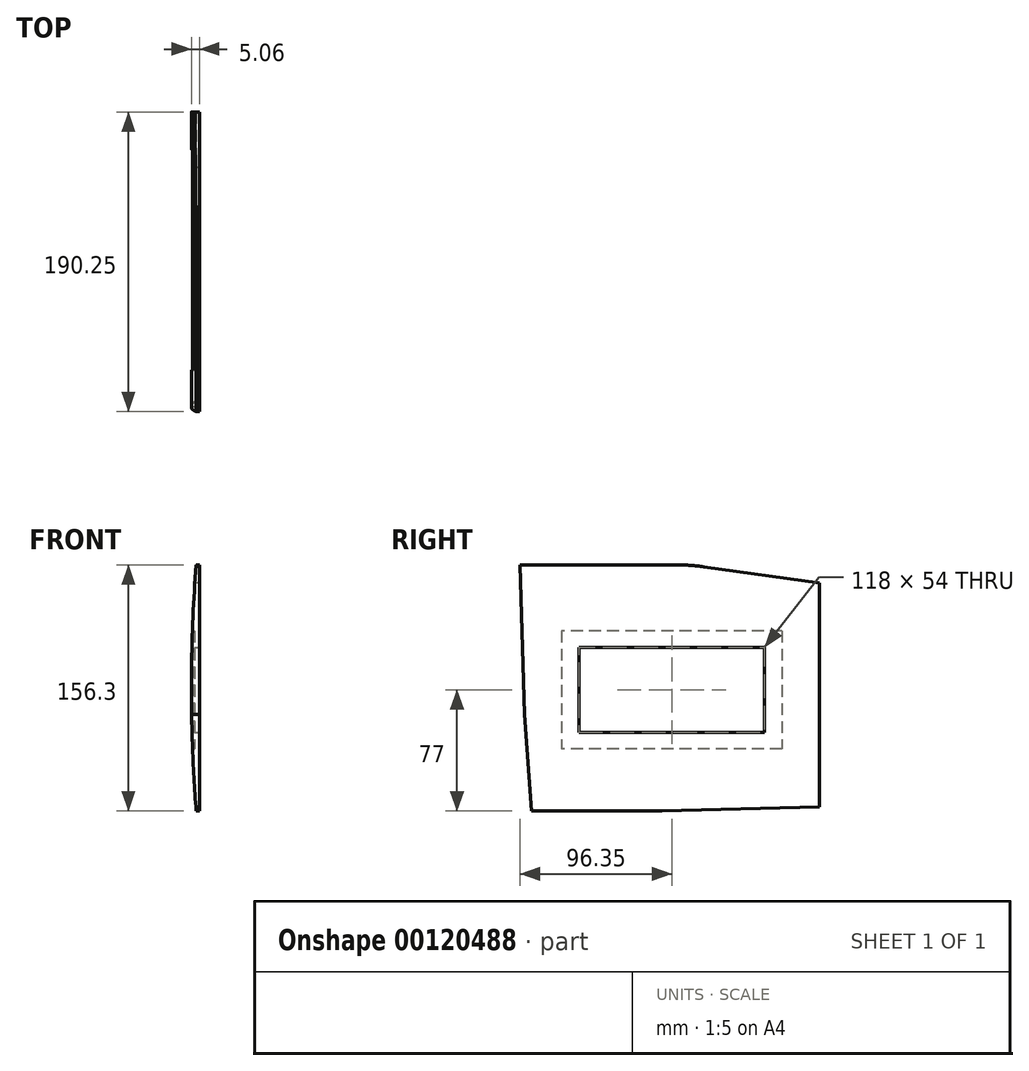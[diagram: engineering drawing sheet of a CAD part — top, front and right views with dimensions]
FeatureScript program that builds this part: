
annotation { "Feature Type Name" : "Feature", "Feature Type Description" : "" }
export const myFeature = defineFeature(function(context is Context, id is Id, definition is map)
    precondition{}
    {
        {
            var Q0;
            Q0=qCreatedBy(makeId("Right.planeOp"),FACE);
            var sketch = newSketch(context, id + "F0", { "sketchPlane" : qUnion([Q0])});
            skLineSegment(sketch, "E0", {"start": v(0, 0) * mm, "end": v(80, 0) * mm});
            skLineSegment(sketch, "E1", {"start": v(0, 0) * mm, "end": v(-4.51, 61.34) * mm});
            skLineSegment(sketch, "E2", {"start": v(82.93, 0.04) * mm, "end": v(182.9, 2.48) * mm});
            skLineSegment(sketch, "E3", {"start": v(192.3, 3.08) * mm, "end": v(237.07, 7.7) * mm});
            skLineSegment(sketch, "E4", {"start": v(-4.51, 61.34) * mm, "end": v(-7.35, 156.3) * mm});
            skLineSegment(sketch, "E5", {"start": v(-7.35, 156.3) * mm, "end": v(92.65, 156.3) * mm});
            skLineSegment(sketch, "E6", {"start": v(109.35, 155.13) * mm, "end": v(193.53, 143.3) * mm});
            skArc(sketch, "E7", {"start": v(237.07, 7.7) * mm, "mid": v(244, 10.86) * mm, "end": v(247.65, 17.55) * mm});
            skPoint(sketch, "E8.visualSharp", {"position": v(101.04, 156.3) * mm});
            skArc(sketch, "E8.filletArc", {"start": v(109.35, 155.13) * mm, "mid": v(101.02, 156) * mm, "end": v(92.65, 156.3) * mm});
            skPoint(sketch, "E9.visualSharp", {"position": v(187.62, 2.6) * mm});
            skArc(sketch, "E9.filletArc", {"start": v(182.9, 2.48) * mm, "mid": v(187.6, 2.69) * mm, "end": v(192.3, 3.08) * mm});
            skPoint(sketch, "E10.visualSharp", {"position": v(81.47, 0) * mm});
            skArc(sketch, "E10.filletArc", {"start": v(80, 0) * mm, "mid": v(81.47, 0) * mm, "end": v(82.93, 0.04) * mm});
            skArc(sketch, "E11", {"start": v(247.65, 17.55) * mm, "mid": v(250.07, 59.77) * mm, "end": v(242.56, 101.4) * mm});
            skArc(sketch, "E12", {"start": v(200.68, 141.85) * mm, "mid": v(197.12, 142.68) * mm, "end": v(193.53, 143.3) * mm});
            skArc(sketch, "E13", {"start": v(242.56, 101.4) * mm, "mid": v(226.86, 127.04) * mm, "end": v(200.68, 141.85) * mm});
            skSolve(sketch);
        }
        {
            var Q0;
            Q0 = qSketchRegion(id + "F0", true);
            extrude(context, id + "F1", {"entities" : qUnion([Q0]), "endBound" : BoundingType.SYMMETRIC, "depth" : 100 * mm});
        }
        {
            var Q0;
            Q0=qCreatedBy(makeId("Front.planeOp"),FACE);
            var sketch = newSketch(context, id + "F2", { "sketchPlane" : qUnion([Q0])});
            skArc(sketch, "E14", {"start": v(0, 156.3) * mm, "mid": v(-3.06, 78.15) * mm, "end": v(0, 0) * mm});
            skArc(sketch, "E15", {"start": v(2, 156.3) * mm, "mid": v(-1.06, 78.15) * mm, "end": v(2, 0) * mm, "construction": true});
            skLineSegment(sketch, "E16", {"start": v(0, 156.3) * mm, "end": v(2, 156.3) * mm, "construction": true});
            skLineSegment(sketch, "E17", {"start": v(0, 0) * mm, "end": v(2, 0) * mm, "construction": true});
            skLineSegment(sketch, "E18", {"start": v(0, 156.3) * mm, "end": v(-64.22, 156.3) * mm});
            skLineSegment(sketch, "E19", {"start": v(-64.22, 156.3) * mm, "end": v(-64.22, 0) * mm});
            skLineSegment(sketch, "E20", {"start": v(-64.22, 0) * mm, "end": v(0, 0) * mm});
            skLineSegment(sketch, "E21", {"start": v(2, 156.3) * mm, "end": v(69.58, 156.3) * mm});
            skLineSegment(sketch, "E22", {"start": v(69.58, 156.3) * mm, "end": v(69.58, 0) * mm});
            skLineSegment(sketch, "E23", {"start": v(69.58, 0) * mm, "end": v(2, 0) * mm});
            skLineSegment(sketch, "E24", {"start": v(2, 156.3) * mm, "end": v(2, 0) * mm});
            skSolve(sketch);
        }
        {
            var Q0;
            Q0 = qSketchRegion(id + "F2", true);
            extrude(context, id + "F3", {"entities" : qUnion([Q0]), "operationType" : NewBodyOperationType.REMOVE, "endBound" : BoundingType.THROUGH_ALL, "oppositeDirection" : true, "depth" : 25 * mm, "hasSecondDirection" : true, "secondDirectionBound" : SecondDirectionBoundingType.THROUGH_ALL, "secondDirectionOppositeDirection" : false, "secondDirectionDepth" : 25 * mm});
        }
        {
            var Q0;
            Q0=qCreatedBy(makeId("Right.planeOp"),FACE);
            var sketch = newSketch(context, id + "F4", { "sketchPlane" : qUnion([Q0])});
            skLineSegment(sketch, "E25.bottom", {"start": v(30, 104) * mm, "end": v(148, 104) * mm});
            skLineSegment(sketch, "E25.top", {"start": v(30, 50) * mm, "end": v(148, 50) * mm});
            skLineSegment(sketch, "E25.left", {"start": v(30, 104) * mm, "end": v(30, 50) * mm});
            skLineSegment(sketch, "E25.right", {"start": v(148, 104) * mm, "end": v(148, 50) * mm});
            skSolve(sketch);
        }
        {
            var Q0;
            Q0 = qSketchRegion(id + "F4", true);
            extrude(context, id + "F5", {"entities" : qUnion([Q0]), "operationType" : NewBodyOperationType.REMOVE, "endBound" : BoundingType.THROUGH_ALL, "oppositeDirection" : true, "depth" : 25 * mm, "hasSecondDirection" : true, "secondDirectionBound" : SecondDirectionBoundingType.THROUGH_ALL, "secondDirectionOppositeDirection" : false, "secondDirectionDepth" : 25 * mm});
        }
        {
            var Q0;
            Q0=makeQuery(id+"F3.boolean.opBoolean","COPY",FACE,{"derivedFrom":makeQuery(id+"F3.opExtrude","SWEPT_FACE",FACE,{"disambiguationData":[OSD([sQuery(id+"F2.wireOp",EDGE,"E24")])]})});
            cPlane(context, id + "F6", {"entities" : qUnion([Q0]), "cplaneType" : CPlaneType.OFFSET, "offset" : 3 * mm, "oppositeDirection" : true, "width" : 150 * mm, "height" : 150 * mm});
        }
        {
            var Q0;
            Q0=qCreatedBy(id+"F6.planeOp",FACE);
            var sketch = newSketch(context, id + "F7", { "sketchPlane" : qUnion([Q0])});
            skLineSegment(sketch, "E26.bottom", {"start": v(159, 114.5) * mm, "end": v(19, 114.5) * mm});
            skLineSegment(sketch, "E26.top", {"start": v(159, 39.5) * mm, "end": v(19, 39.5) * mm});
            skLineSegment(sketch, "E26.left", {"start": v(159, 114.5) * mm, "end": v(159, 39.5) * mm});
            skLineSegment(sketch, "E26.right", {"start": v(19, 114.5) * mm, "end": v(19, 39.5) * mm});
            skPoint(sketch, "E26.middle", {"position": v(89, 77) * mm});
            skLineSegment(sketch, "E27", {"start": v(148, 50) * mm, "end": v(30, 104) * mm, "construction": true});
            skSolve(sketch);
        }
        {
            var Q0;
            Q0 = qSketchRegion(id + "F7", true);
            extrude(context, id + "F8", {"entities" : qUnion([Q0]), "operationType" : NewBodyOperationType.REMOVE, "oppositeDirection" : true, "depth" : 25 * mm});
        }
        {
            var Q0;
            Q0=makeQuery(id+"F3.boolean.opBoolean","COPY",FACE,{"derivedFrom":makeQuery(id+"F3.opExtrude","SWEPT_FACE",FACE,{"disambiguationData":[OSD([sQuery(id+"F2.wireOp",EDGE,"E24")])]})});
            var sketch = newSketch(context, id + "F9", { "sketchPlane" : qUnion([Q0])});
            skLineSegment(sketch, "E28.bottom", {"start": v(182.9, 2.48) * mm, "end": v(270.46, 2.48) * mm});
            skLineSegment(sketch, "E28.top", {"start": v(182.9, 198.71) * mm, "end": v(270.46, 198.71) * mm});
            skLineSegment(sketch, "E28.left", {"start": v(182.9, 2.48) * mm, "end": v(182.9, 198.71) * mm});
            skLineSegment(sketch, "E28.right", {"start": v(270.46, 2.48) * mm, "end": v(270.46, 198.71) * mm});
            skSolve(sketch);
        }
        {
            var Q0;
            Q0 = qSketchRegion(id + "F9", true);
            extrude(context, id + "F10", {"entities" : qUnion([Q0]), "operationType" : NewBodyOperationType.REMOVE, "endBound" : BoundingType.THROUGH_ALL, "oppositeDirection" : true, "depth" : 25 * mm});
        }
    });
